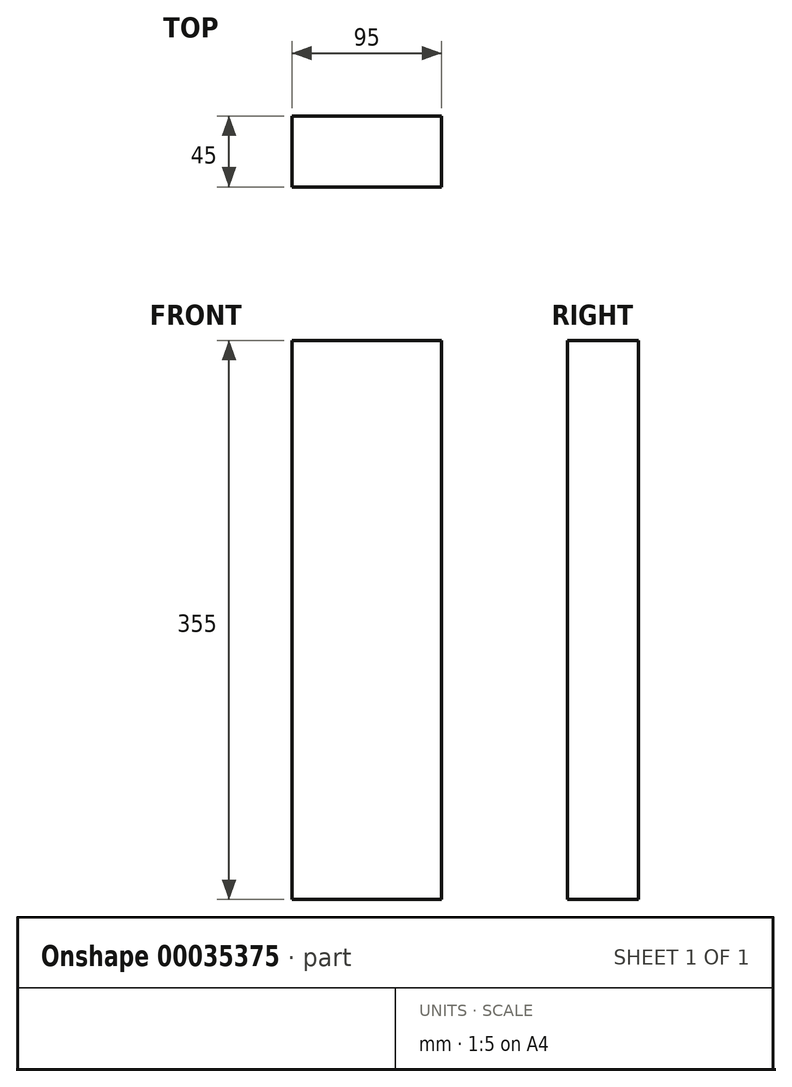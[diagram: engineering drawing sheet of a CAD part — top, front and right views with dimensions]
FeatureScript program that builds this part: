
annotation { "Feature Type Name" : "Feature", "Feature Type Description" : "" }
export const myFeature = defineFeature(function(context is Context, id is Id, definition is map)
    precondition{}
    {
        {
            var Q0;
            Q0=qCreatedBy(makeId("Top.planeOp"),FACE);
            var sketch = newSketch(context, id + "F0", { "sketchPlane" : qUnion([Q0])});
            skLineSegment(sketch, "E0.rect.bottom", {"start": v(47.5, -22.5) * mm, "end": v(-47.5, -22.5) * mm});
            skLineSegment(sketch, "E0.rect.top", {"start": v(47.5, 22.5) * mm, "end": v(-47.5, 22.5) * mm});
            skLineSegment(sketch, "E0.rect.left", {"start": v(47.5, -22.5) * mm, "end": v(47.5, 22.5) * mm});
            skLineSegment(sketch, "E0.rect.right", {"start": v(-47.5, -22.5) * mm, "end": v(-47.5, 22.5) * mm});
            skPoint(sketch, "E0.rect.middle", {"position": v(0, 0) * mm});
            skSolve(sketch);
        }
        {
            var Q0;
            Q0=makeQuery(id+"F0.imprint","IMPRINT",FACE,{"disambiguationData":[TD([[makeQuery(id+"F0.imprint","IMPRINT",EDGE,{"derivedFrom":sQuery(id+"F0.wireOp",EDGE,"E0.rect.bottom")}),-1.0]])]});
            extrude(context, id + "F1", {"entities" : qUnion([Q0]), "depth" : 355 * mm});
        }
    });
